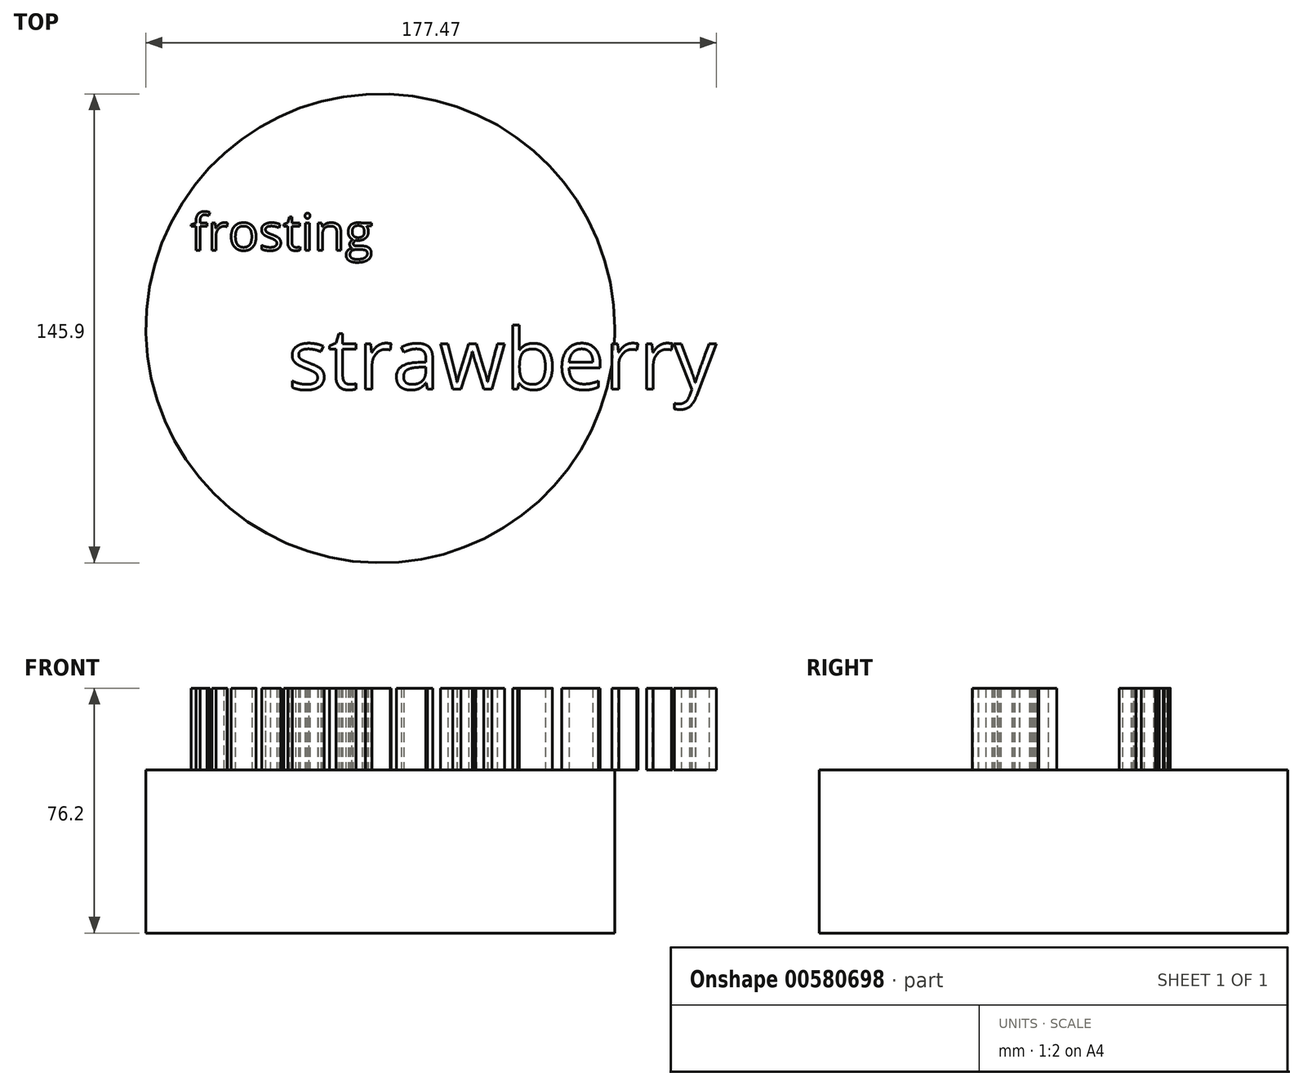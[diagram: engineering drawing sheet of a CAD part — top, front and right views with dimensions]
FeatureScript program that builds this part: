
annotation { "Feature Type Name" : "Feature", "Feature Type Description" : "" }
export const myFeature = defineFeature(function(context is Context, id is Id, definition is map)
    precondition{}
    {
        {
            var Q0;
            Q0=qCreatedBy(makeId("Top.planeOp"),FACE);
            var sketch = newSketch(context, id + "F0", { "sketchPlane" : qUnion([Q0])});
            skCircle(sketch, "E0", {"center": v(0, 0) * mm, "radius": 72.95 * mm});
            skSolve(sketch);
        }
        {
            var Q0;
            Q0=makeQuery(id+"F0.imprint","IMPRINT",FACE,{"disambiguationData":[TD([[makeQuery(id+"F0.imprint","IMPRINT",EDGE,{"derivedFrom":sQuery(id+"F0.wireOp",EDGE,"E0")}),1.0]])]});
            extrude(context, id + "F1", {"entities" : qUnion([Q0]), "oppositeDirection" : true, "depth" : 25.4 * mm, "offsetDistance" : 25.4 * mm});
        }
        {
            var Q0;
            Q0=makeQuery(id+"F1.opExtrude","CAP_FACE",FACE,{"disambiguationData":[OSD([sQuery(id+"F0.wireOp",EDGE,"E0")])],"isStart":false});
            extrude(context, id + "F2", {"entities" : qUnion([Q0]), "operationType" : NewBodyOperationType.ADD, "depth" : 25.4 * mm, "offsetDistance" : 25.4 * mm});
        }
        {
            var Q0;
            Q0=qCreatedBy(makeId("Top.planeOp"),FACE);
            var sketch = newSketch(context, id + "F3", { "sketchPlane" : qUnion([Q0])});
            skText(sketch, "E1", { "text": "strawberry", "fontName": "OpenSans-Regular.ttf"});
            const initialGuessF3  = {"E1": [-0.0288, -0.01895, 1, 0, 0.01895]};
            skSetInitialGuess(sketch, initialGuessF3);
            skSolve(sketch);
        }
        {
            var Q0;
            Q0 = qSketchRegion(id + "F3", true);
            extrude(context, id + "F4", {"entities" : qUnion([Q0]), "operationType" : NewBodyOperationType.ADD, "depth" : 25.4 * mm, "offsetDistance" : 25.4 * mm});
        }
        {
            var Q0;
            {var subQ0=sQuery(id+"F0.wireOp",EDGE,"E0");Q0=makeQuery(id+"F4.boolean.opBoolean","SPLIT",FACE,{"disambiguationData":[TD([makeQuery(id+"F1.opExtrude","SWEPT_FACE",FACE,{"disambiguationData":[OSD([subQ0])]})])],"derivedFrom":makeQuery(id+"F1.opExtrude","CAP_FACE",FACE,{"disambiguationData":[OSD([subQ0])],"isStart":true})});}
            var sketch = newSketch(context, id + "F5", { "sketchPlane" : qUnion([Q0])});
            skText(sketch, "E2", { "text": "frosting", "fontName": "OpenSans-Regular.ttf"});
            const initialGuessF5  = {"E2": [-0.05911, 0.0243, 1, 0, 0.01137]};
            skSetInitialGuess(sketch, initialGuessF5);
            skSolve(sketch);
        }
        {
            var Q0;
            Q0 = qSketchRegion(id + "F5", true);
            extrude(context, id + "F6", {"entities" : qUnion([Q0]), "operationType" : NewBodyOperationType.ADD, "depth" : 25.4 * mm, "offsetDistance" : 25.4 * mm});
        }
    });
